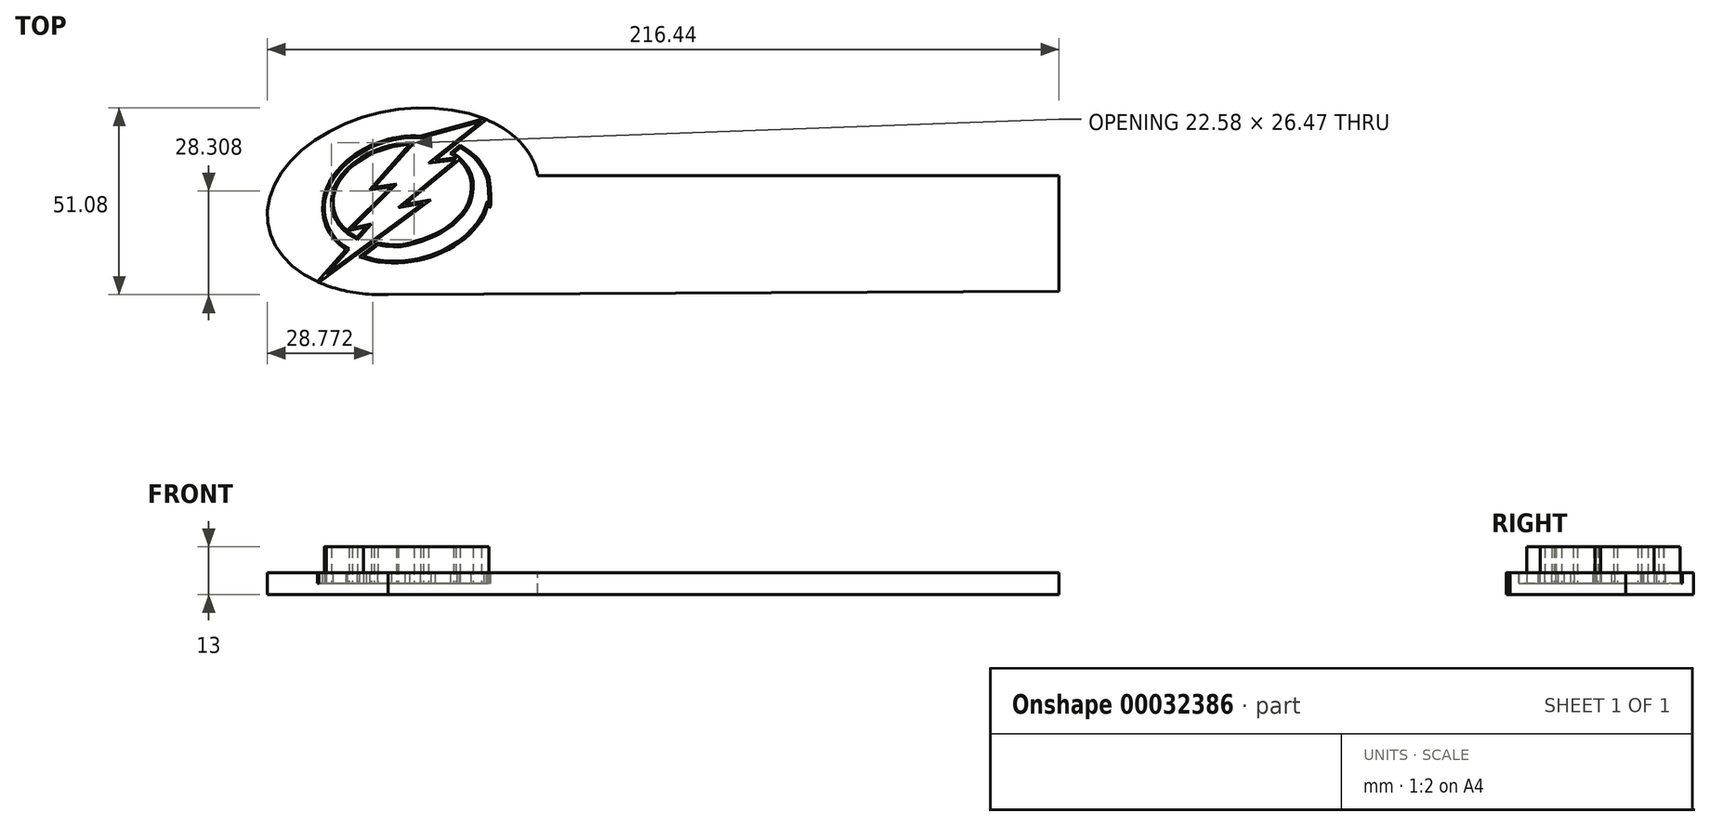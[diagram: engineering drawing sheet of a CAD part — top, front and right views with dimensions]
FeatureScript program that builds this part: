
annotation { "Feature Type Name" : "Feature", "Feature Type Description" : "" }
export const myFeature = defineFeature(function(context is Context, id is Id, definition is map)
    precondition{}
    {
        {
            var Q0;
            Q0=qCreatedBy(makeId("Top.planeOp"),FACE);
            var sketch = newSketch(context, id + "F0", { "sketchPlane" : qUnion([Q0])});
            skLineSegment(sketch, "E0", {"start": v(0.6, -41.88) * mm, "end": v(27.12, -22.36) * mm});
            skLineSegment(sketch, "E1", {"start": v(27.12, -22.36) * mm, "end": v(20.32, -23.56) * mm});
            skLineSegment(sketch, "E2", {"start": v(20.32, -23.56) * mm, "end": v(36.07, -10.48) * mm});
            skLineSegment(sketch, "E3", {"start": v(36.07, -10.48) * mm, "end": v(28.58, -11.43) * mm});
            skLineSegment(sketch, "E4", {"start": v(28.58, -11.43) * mm, "end": v(42.95, 0) * mm});
            skLineSegment(sketch, "E5", {"start": v(42.95, 0) * mm, "end": v(26.34, -4.54) * mm});
            skLineSegment(sketch, "E6", {"start": v(24.53, -5.84) * mm, "end": v(13.69, -18.05) * mm});
            skLineSegment(sketch, "E7", {"start": v(13.69, -18.05) * mm, "end": v(19.8, -17.1) * mm});
            skLineSegment(sketch, "E8", {"start": v(19.8, -17.1) * mm, "end": v(7.66, -29.16) * mm});
            skLineSegment(sketch, "E9", {"start": v(7.66, -29.16) * mm, "end": v(12.92, -28.05) * mm});
            skLineSegment(sketch, "E10", {"start": v(12.92, -28.05) * mm, "end": v(9.12, -32.3) * mm});
            skFitSpline(sketch, "E11", {"points": [v(35.36, -8.71) * mm, v(37.98, -10.92) * mm, v(40.46, -15.13) * mm, v(40.55, -19.95) * mm, v(39.17, -23.9) * mm, v(36.24, -27.35) * mm, v(32.71, -30.1) * mm, v(29.18, -31.82) * mm, v(24.45, -33.46) * mm, v(19.89, -34.32) * mm, v(14.75, -33.81) * mm], "startDerivative": vector(33.63, -20.1) * mm, "endDerivative": vector(-46.98, 7.07) * mm});
            skFitSpline(sketch, "E12", {"points": [v(37.21, -7.09) * mm, v(39.5, -8.64) * mm, v(40.94, -9.87) * mm, v(42.18, -11.23) * mm, v(43.92, -13.98) * mm, v(44.74, -16.32) * mm, v(45.04, -21.22) * mm, v(45.04, -23.12) * mm, v(44.79, -21.62) * mm, v(43.44, -25.3) * mm, v(42, -27.57) * mm, v(40.25, -29.66) * mm, v(37.49, -32.18) * mm, v(35.25, -33.67) * mm, v(33.23, -34.88) * mm, v(28.23, -36.9) * mm, v(22.27, -38.07) * mm, v(17.84, -38.18) * mm, v(14.64, -37.9) * mm, v(10.7, -36.86) * mm], "startDerivative": vector(48, -31.13) * mm, "endDerivative": vector(-66.23, 19.7) * mm});
            skLineSegment(sketch, "E13", {"start": v(14.75, -33.81) * mm, "end": v(10.7, -36.86) * mm});
            skLineSegment(sketch, "E14", {"start": v(37.21, -7.09) * mm, "end": v(35.36, -8.71) * mm});
            skFitSpline(sketch, "E15", {"points": [v(9.12, -32.3) * mm, v(7.97, -31.68) * mm, v(6.36, -30.6) * mm, v(4.44, -28.78) * mm, v(3.4, -27.31) * mm, v(2.61, -25.75) * mm, v(2.23, -24.63) * mm, v(1.96, -23) * mm, v(2, -21.34) * mm, v(2.37, -19.15) * mm, v(3.38, -16.77) * mm, v(4.74, -14.7) * mm, v(7.23, -12.01) * mm, v(11.3, -9.2) * mm, v(14.07, -7.88) * mm, v(17.32, -6.8) * mm, v(20.63, -6.1) * mm, v(24.53, -5.84) * mm], "startDerivative": vector(-25.4, 12.77) * mm, "endDerivative": vector(54, 2.21) * mm});
            skFitSpline(sketch, "E16", {"points": [v(26.34, -4.54) * mm, v(24.7, -4.44) * mm, v(22.46, -4.54) * mm, v(18.96, -5.07) * mm, v(16.74, -5.64) * mm, v(14.61, -6.4) * mm, v(12.38, -7.31) * mm, v(10.57, -8.33) * mm, v(9.12, -9.18) * mm, v(7.71, -10.2) * mm, v(6.57, -11.15) * mm, v(5.06, -12.55) * mm, v(3.73, -14.07) * mm, v(2.67, -15.51) * mm, v(2.2, -16.28) * mm, v(1.43, -17.6) * mm, v(0.98, -18.71) * mm, v(0.4, -20.7) * mm, v(0.15, -22.1) * mm, v(0.1, -23.17) * mm, v(0.1, -25.02) * mm, v(0.28, -26.3) * mm, v(0.88, -28.34) * mm, v(1.74, -30.04) * mm, v(2.62, -31.35) * mm, v(3.82, -32.69) * mm, v(5.84, -34.39) * mm, v(6.77, -34.95) * mm], "startDerivative": vector(-45.39, 3.92) * mm, "endDerivative": vector(29, -15.48) * mm});
            skLineSegment(sketch, "E17.trimOffspring", {"start": v(6.77, -34.95) * mm, "end": v(0.6, -41.88) * mm});
            skSolve(sketch);
        }
        {
            var Q0;
            Q0=makeQuery(id+"F0.imprint","IMPRINT",FACE,{"disambiguationData":[TD([[makeQuery(id+"F0.imprint","IMPRINT",EDGE,{"derivedFrom":sQuery(id+"F0.wireOp",EDGE,"E0")}),1.0]])]});
            var Q1;
            Q1=makeQuery(id+"F0.imprint","IMPRINT",FACE,{"disambiguationData":[TD([[makeQuery(id+"F0.imprint","IMPRINT",EDGE,{"derivedFrom":sQuery(id+"F0.wireOp",EDGE,"E11")}),1.0]])]});
            extrude(context, id + "F1", {"entities" : qUnion([Q0, Q1]), "depth" : 10 * mm});
        }
        {
            var Q0;
            Q0=qCreatedBy(makeId("Top.planeOp"),FACE);
            var sketch = newSketch(context, id + "F2", { "sketchPlane" : qUnion([Q0])});
            skLineSegment(sketch, "E18", {"start": v(0, -25.96) * mm, "end": v(58.44, -14.82) * mm});
            skEllipticalArc(sketch, "E19", {});
            skLineSegment(sketch, "E20", {"start": v(58.44, -14.82) * mm, "end": v(200.9, -14.82) * mm});
            skLineSegment(sketch, "E21", {"start": v(200.9, -14.82) * mm, "end": v(200.9, -46.45) * mm});
            skLineSegment(sketch, "E22", {"start": v(17.52, -47.36) * mm, "end": v(200.9, -46.45) * mm});
            skPoint(sketch, "E22.endSnap0", {"position": v(26.28, -46.4) * mm});
            const initialGuessF2  = {"E19": [0.021598979321428957, -0.02183913742614852, 0.9823232658764951, 0.18719241789596264, 0.0375, 0.025, 0, 4.71238898038469]};
            skSetInitialGuess(sketch, initialGuessF2);
            skSolve(sketch);
        }
        {
            var Q0;
            Q0=makeQuery(id+"F2.imprint","IMPRINT",FACE,{"disambiguationData":[TD([[makeQuery(id+"F2.imprint","IMPRINT",EDGE,{"derivedFrom":sQuery(id+"F2.wireOp",EDGE,"E19")}),1.0]])]});
            extrude(context, id + "F3", {"entities" : qUnion([Q0]), "oppositeDirection" : true, "depth" : 6 * mm});
        }
        {
            var Q0;
            Q0=makeQuery(id+"F3.opExtrude","SWEPT_BODY",BODY,{"disambiguationData":[OSD([sQuery(id+"F2.wireOp",EDGE,"E19")])]});
            var Q1;
            Q1=qCreatedBy(makeId("Top.planeOp"),FACE);
            transform(context, id + "F4", {"entities" : qUnion([Q0]), "transformType" : TransformType.TRANSLATION_DISTANCE, "transformDirection" : qUnion([Q1]), "distance" : 3 * mm, "makeCopy" : false});
        }
        {
            var Q0;
            Q0=makeQuery(id+"F1.opExtrude","SWEPT_BODY",BODY,{"disambiguationData":[OSD([sQuery(id+"F0.wireOp",EDGE,"E0"),sQuery(id+"F0.wireOp",EDGE,"E1"),sQuery(id+"F0.wireOp",EDGE,"E2"),sQuery(id+"F0.wireOp",EDGE,"E3"),sQuery(id+"F0.wireOp",EDGE,"E4"),sQuery(id+"F0.wireOp",EDGE,"E5"),sQuery(id+"F0.wireOp",EDGE,"E6"),sQuery(id+"F0.wireOp",EDGE,"E7"),sQuery(id+"F0.wireOp",EDGE,"E8"),sQuery(id+"F0.wireOp",EDGE,"E9"),sQuery(id+"F0.wireOp",EDGE,"E10"),sQuery(id+"F0.wireOp",EDGE,"E15"),sQuery(id+"F0.wireOp",EDGE,"E16"),sQuery(id+"F0.wireOp",EDGE,"E17.trimOffspring")])]});
            var Q1;
            Q1=makeQuery(id+"F1.opExtrude","SWEPT_BODY",BODY,{"disambiguationData":[OSD([sQuery(id+"F0.wireOp",EDGE,"E11"),sQuery(id+"F0.wireOp",EDGE,"E12"),sQuery(id+"F0.wireOp",EDGE,"E13"),sQuery(id+"F0.wireOp",EDGE,"E14")])]});
            var Q2;
            Q2=makeQuery(id+"F3.opExtrude","SWEPT_BODY",BODY,{"disambiguationData":[OSD([sQuery(id+"F2.wireOp",EDGE,"E19")])]});
            var Q3;
            Q3=makeQuery(id+"F1.opExtrude","SWEPT_FACE",FACE,{"disambiguationData":[OSD([sQuery(id+"F0.wireOp",EDGE,"E16")])]});
            var Q4;
            Q4=makeQuery(id+"F1.opExtrude","SWEPT_FACE",FACE,{"disambiguationData":[OSD([sQuery(id+"F0.wireOp",EDGE,"E17.trimOffspring")])]});
            var Q5;
            Q5=makeQuery(id+"F1.opExtrude","SWEPT_FACE",FACE,{"disambiguationData":[OSD([sQuery(id+"F0.wireOp",EDGE,"E0")])]});
            var Q6;
            Q6=makeQuery(id+"F1.opExtrude","SWEPT_FACE",FACE,{"disambiguationData":[OSD([sQuery(id+"F0.wireOp",EDGE,"E2")])]});
            var Q7;
            Q7=makeQuery(id+"F1.opExtrude","SWEPT_FACE",FACE,{"disambiguationData":[OSD([sQuery(id+"F0.wireOp",EDGE,"E4")])]});
            var Q8;
            Q8=makeQuery(id+"F1.opExtrude","SWEPT_FACE",FACE,{"disambiguationData":[OSD([sQuery(id+"F0.wireOp",EDGE,"E7")])]});
            var Q9;
            Q9=makeQuery(id+"F1.opExtrude","SWEPT_FACE",FACE,{"disambiguationData":[OSD([sQuery(id+"F0.wireOp",EDGE,"E9")])]});
            var Q10;
            Q10=makeQuery(id+"F1.opExtrude","SWEPT_FACE",FACE,{"disambiguationData":[OSD([sQuery(id+"F0.wireOp",EDGE,"E15")])]});
            var Q11;
            Q11=makeQuery(id+"F1.opExtrude","SWEPT_FACE",FACE,{"disambiguationData":[OSD([sQuery(id+"F0.wireOp",EDGE,"E11")])]});
            var Q12;
            Q12=makeQuery(id+"F1.opExtrude","SWEPT_FACE",FACE,{"disambiguationData":[OSD([sQuery(id+"F0.wireOp",EDGE,"E12")])]});
            var Q13;
            Q13=makeQuery(id+"F1.opExtrude","SWEPT_FACE",FACE,{"disambiguationData":[OSD([sQuery(id+"F0.wireOp",EDGE,"E13")])]});
            var Q14;
            Q14=makeQuery(id+"F1.opExtrude","SWEPT_FACE",FACE,{"disambiguationData":[OSD([sQuery(id+"F0.wireOp",EDGE,"E8")])]});
            var Q15;
            Q15=makeQuery(id+"F1.opExtrude","SWEPT_FACE",FACE,{"disambiguationData":[OSD([sQuery(id+"F0.wireOp",EDGE,"E10")])]});
            var Q16;
            Q16=makeQuery(id+"F1.opExtrude","SWEPT_FACE",FACE,{"disambiguationData":[OSD([sQuery(id+"F0.wireOp",EDGE,"E1")])]});
            var Q17;
            Q17=makeQuery(id+"F1.opExtrude","SWEPT_FACE",FACE,{"disambiguationData":[OSD([sQuery(id+"F0.wireOp",EDGE,"E14")])]});
            var Q18;
            Q18=makeQuery(id+"F1.opExtrude","SWEPT_FACE",FACE,{"disambiguationData":[OSD([sQuery(id+"F0.wireOp",EDGE,"E6")])]});
            var Q19;
            Q19=makeQuery(id+"F1.opExtrude","SWEPT_FACE",FACE,{"disambiguationData":[OSD([sQuery(id+"F0.wireOp",EDGE,"E5")])]});
            var Q20;
            Q20=makeQuery(id+"F1.opExtrude","SWEPT_FACE",FACE,{"disambiguationData":[OSD([sQuery(id+"F0.wireOp",EDGE,"E3")])]});
            booleanBodies(context, id + "F5", {"operationType" : BooleanOperationType.SUBTRACTION, "tools" : qUnion([Q0, Q1]), "targets" : qUnion([Q2]), "offset" : true, "entitiesToOffset" : qUnion([Q3, Q4, Q5, Q6, Q7, Q8, Q9, Q10, Q11, Q12, Q13, Q14, Q15, Q16, Q17, Q18, Q19, Q20]), "offsetDistance" : .5 * mm, "keepTools" : true});
        }
    });
